# Revit family: Kohler Composed 73078T-4E-CP Family
name_source: partatom
category: Plumbing Fixtures
revit_build: Autodesk Revit 2018 (Build: 20181011_1500(x64)
units: mm (PartAtom-declared; Revit-internal decimal feet)

## family parameters
Cut with Voids When Loaded = No
Host = Face
OmniClass Number = 23.45.55.00
OmniClass Title = Sanitary Faucets, Wastes
Part Type = Normal
Room Calculation Point = No
Round Connector Dimension = Use Diameter
Shared = No

## types (2) — shared parameters
CW Connection = Yes
Cold Water Inlet = Cold Water Inlet
Default Elevation = 914 mm
Description = Single-handle deck-mount bath faucet with handshower
Disclaimer = Although care has been taken to ensure, to the best of our knowledge, that all data and information contained herein is accurate to the extent that it relates to either matters of fact or accepted practice at the time of issue. MDFC (Pty) Ltd assumes no responsibility for any errors in, or misinterpretation of, such data and/ or information or any loss or damage arising from, or related to its use.
Drain Included = No
Faucet Hole Spacing = 292 mm
Flow Rate = 8 GPM
HW Connection = Yes
Handle Clearance = 49 mm
Height = 232 mm
Hot Water Inlet = Hot Water Inlet
Length = 275 mm
Manufacturer = KOHLER Co.
Material = Premium Metal Construction
Model = Kohler Composed 73078T-4E-CP
Pressure = 45.00 psi
Spout Reach = 210 mm
Telephone = 011 050 9000
Vent Connection = No
Waste Connection = No
Waste Water Outlet = Waste Water Outlet
Width = 356 mm

## per-type parameters (varying)
| type | Assembly Code | Finish | Type | URL |
| Kohler Composed 73078T-4E-CP |  | Kohler-Metal-CP-Polished_Chrome | 1 | www.africa.kohler.com |
| TT-Vibrant Titanium | D2010 | Kohler-Metal-TT-Vibrant_Titanium | 2 | https://www.us.kohler.com |

## geometry (parser evidence)
native form markers: Sweep x8
no freeform markers — native parametric forms only
